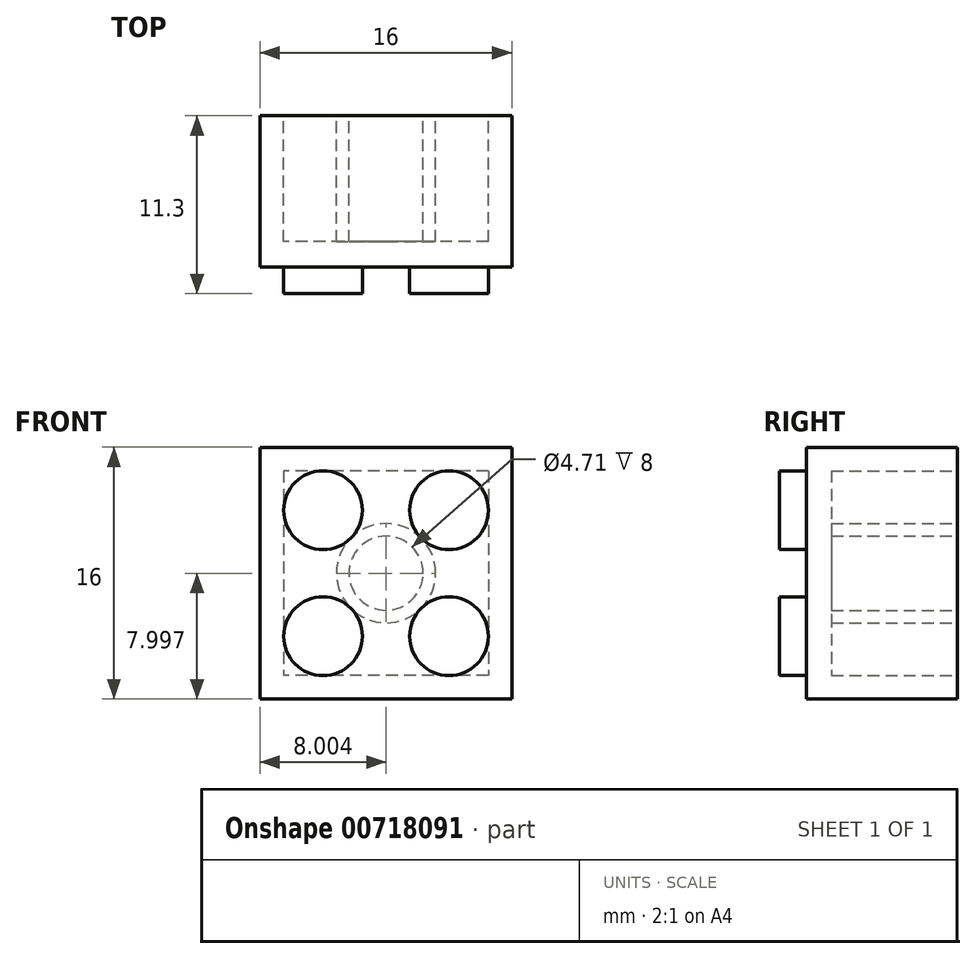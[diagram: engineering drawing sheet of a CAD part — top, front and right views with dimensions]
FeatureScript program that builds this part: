
annotation { "Feature Type Name" : "Feature", "Feature Type Description" : "" }
export const myFeature = defineFeature(function(context is Context, id is Id, definition is map)
    precondition{}
    {
        {
            var Q0;
            Q0=qCreatedBy(makeId("Front.planeOp"),FACE);
            var sketch = newSketch(context, id + "F0", { "sketchPlane" : qUnion([Q0])});
            skLineSegment(sketch, "E0.bottom", {"start": v(-19.26, -38.43) * mm, "end": v(-3.26, -38.43) * mm});
            skLineSegment(sketch, "E0.top", {"start": v(-19.26, -54.43) * mm, "end": v(-3.26, -54.43) * mm});
            skLineSegment(sketch, "E0.left", {"start": v(-19.26, -38.43) * mm, "end": v(-19.26, -54.43) * mm});
            skLineSegment(sketch, "E0.right", {"start": v(-3.26, -38.43) * mm, "end": v(-3.26, -54.43) * mm});
            skSolve(sketch);
        }
        {
            var Q0;
            Q0 = qSketchRegion(id + "F0", true);
            extrude(context, id + "F1", {"entities" : qUnion([Q0]), "oppositeDirection" : true, "depth" : 9.6 * mm, "offsetDistance" : 25 * mm});
        }
        {
            var Q0;
            Q0=makeQuery(id+"F1.opExtrude","CAP_FACE",FACE,{"disambiguationData":[OSD([sQuery(id+"F0.wireOp",EDGE,"E0.bottom"),sQuery(id+"F0.wireOp",EDGE,"E0.top"),sQuery(id+"F0.wireOp",EDGE,"E0.left"),sQuery(id+"F0.wireOp",EDGE,"E0.right")])],"isStart":true});
            var sketch = newSketch(context, id + "F2", { "sketchPlane" : qUnion([Q0])});
            skCircle(sketch, "E1", {"center": v(-15.26, -42.43) * mm, "radius": 2.5 * mm});
            skCircle(sketch, "E2", {"center": v(-15.26, -50.43) * mm, "radius": 2.5 * mm});
            skCircle(sketch, "E3", {"center": v(-7.26, -42.43) * mm, "radius": 2.5 * mm});
            skCircle(sketch, "E4", {"center": v(-7.26, -50.43) * mm, "radius": 2.5 * mm});
            skSolve(sketch);
        }
        {
            var Q0;
            Q0 = qSketchRegion(id + "F2", true);
            extrude(context, id + "F3", {"entities" : qUnion([Q0]), "operationType" : NewBodyOperationType.ADD, "depth" : 1.7 * mm, "offsetDistance" : 25 * mm});
        }
        {
            var Q0;
            Q0=makeQuery(id+"F1.opExtrude","CAP_FACE",FACE,{"disambiguationData":[OSD([sQuery(id+"F0.wireOp",EDGE,"E0.bottom"),sQuery(id+"F0.wireOp",EDGE,"E0.top"),sQuery(id+"F0.wireOp",EDGE,"E0.left"),sQuery(id+"F0.wireOp",EDGE,"E0.right")])],"isStart":false});
            var sketch = newSketch(context, id + "F4", { "sketchPlane" : qUnion([Q0])});
            skLineSegment(sketch, "E5.bottom", {"start": v(4.76, -39.93) * mm, "end": v(17.76, -39.93) * mm});
            skLineSegment(sketch, "E5.top", {"start": v(4.76, -52.93) * mm, "end": v(17.76, -52.93) * mm});
            skLineSegment(sketch, "E5.left", {"start": v(4.76, -39.93) * mm, "end": v(4.76, -52.93) * mm});
            skLineSegment(sketch, "E5.right", {"start": v(17.76, -39.93) * mm, "end": v(17.76, -52.93) * mm});
            skCircle(sketch, "E6", {"center": v(11.26, -46.43) * mm, "radius": 3.15 * mm});
            skCircle(sketch, "E7", {"center": v(11.26, -46.43) * mm, "radius": 2.35 * mm});
            skSolve(sketch);
        }
        {
            var Q0;
            Q0 = qSketchRegion(id + "F4", true);
            var Q1;
            Q1=makeQuery(id+"F4.imprint","IMPRINT",FACE,{"disambiguationData":[TD([[makeQuery(id+"F4.imprint","IMPRINT",EDGE,{"derivedFrom":sQuery(id+"F4.wireOp",EDGE,"E7")}),1.0]])]});
            extrude(context, id + "F5", {"entities" : qUnion([Q0, Q1]), "operationType" : NewBodyOperationType.REMOVE, "oppositeDirection" : true, "depth" : 8 * mm, "offsetDistance" : 25 * mm});
        }
    });
